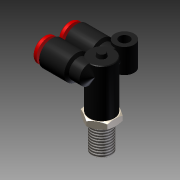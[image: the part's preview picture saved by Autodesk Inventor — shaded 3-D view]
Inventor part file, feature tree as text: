
AUTODESK INVENTOR PART (.ipt)
format: ipt  version: 2012 (Build 160160000, 160)  size: 739,840 bytes
history: native  units: in
note: dims shown in document units (in); Inventor stores cm internally (conversion verified against a paired STEP export)
features: extrude x4, sketch x4, chamfer x3, plane x3, split x3, thread x2, other x1, move_body x1, imported_body x1
ambient origin geometry x8: Origin, YZ Plane, XZ Plane, XY Plane, X Axis, Y Axis, Z Axis, Center Point
bodies: Solid1 (feature_tree), Solid2 (feature_tree), Solid3 (feature_tree), Solid4 (feature_tree), Solid5 (feature_tree), Solid6 (feature_tree), Solid7 (feature_tree)
feature tree (22):
  other  "KQ2LU04-M6.SAT1"
  extrude  "Extrusion1"  Depth=0.1575in TaperAngle=0.0deg
  extrude  "Extrusion2"  Depth=0.1181in TaperAngle=0.0deg
  extrude  "Extrusion3"  Depth=0.0197in TaperAngle=0.0deg
  extrude  "Extrusion4"  Depth=0.3937in TaperAngle=0.0deg
  chamfer  "Chamfer1"  Distance=0.3937in
  thread  "Thread1"  [1 undecoded]
  thread  "Thread2"  [1 undecoded]
  chamfer  "Chamfer2"  [1 undecoded]
  chamfer  "Chamfer3"  [1 undecoded]
  plane  "Work Plane1"
  plane  "Work Plane2"
  split  "Split1"
  split  "Split2"
  move_body  "Move Body1"
  plane  "Work Plane3"
  split  "Split3"
  imported_body  "Base1"
  sketch  "Sketch1"  dims[d0=0.3937in d1=0.0in d2=0.1575in d3=0.0in]
  sketch  "Sketch2"  dims[d4=0.0394in d5=0.1181in d6=0.0in]
  sketch  "Sketch3"  dims[d7=0.0787in d8=0.0197in d9=0.0in]
  sketch  "Sketch4"  dims[d11=0.0157in d12=0.0787in d13=45.0deg d14=0.3937in d15=0.0in d16=0.3937in d17=0.0in d18=0.0157in d19=0.0787in d20=45.0deg d21=0.0079in d22=0.0787in d23=45.0deg d24=0.0in d25=0.0in d26=0.0in d27=-0.1575in d28=0.0in d29=0.0in]
note: 4 required parameter values undecoded (feature->parameter linkage not recoverable at this tier; creation-order binding heuristic only, values carry confidence <= 0.55)
